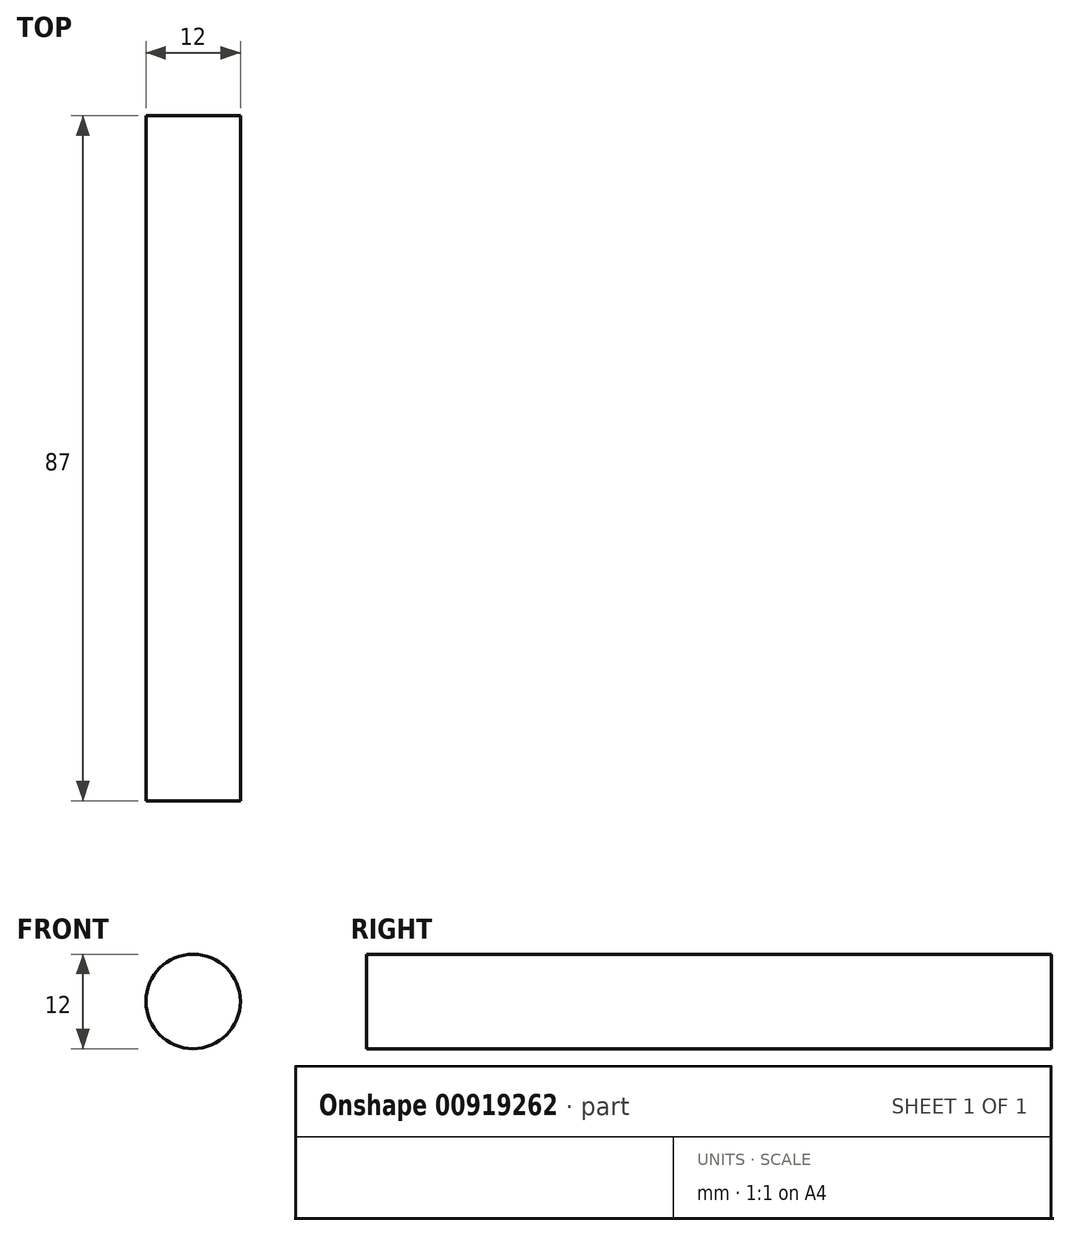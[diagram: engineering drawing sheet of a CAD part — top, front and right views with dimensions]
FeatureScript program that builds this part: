
annotation { "Feature Type Name" : "Feature", "Feature Type Description" : "" }
export const myFeature = defineFeature(function(context is Context, id is Id, definition is map)
    precondition{}
    {
        {
            var Q0;
            Q0=qCreatedBy(makeId("Front.planeOp"),FACE);
            var sketch = newSketch(context, id + "F0", { "sketchPlane" : qUnion([Q0])});
            skCircle(sketch, "E0", {"center": v(0, 0) * mm, "radius": 6 * mm});
            skSolve(sketch);
        }
        {
            var Q0;
            Q0 = qSketchRegion(id + "F0", true);
            extrude(context, id + "F1", {"entities" : qUnion([Q0]), "endBound" : BoundingType.SYMMETRIC, "depth" : 87 * mm, "offsetDistance" : 25 * mm});
        }
    });
